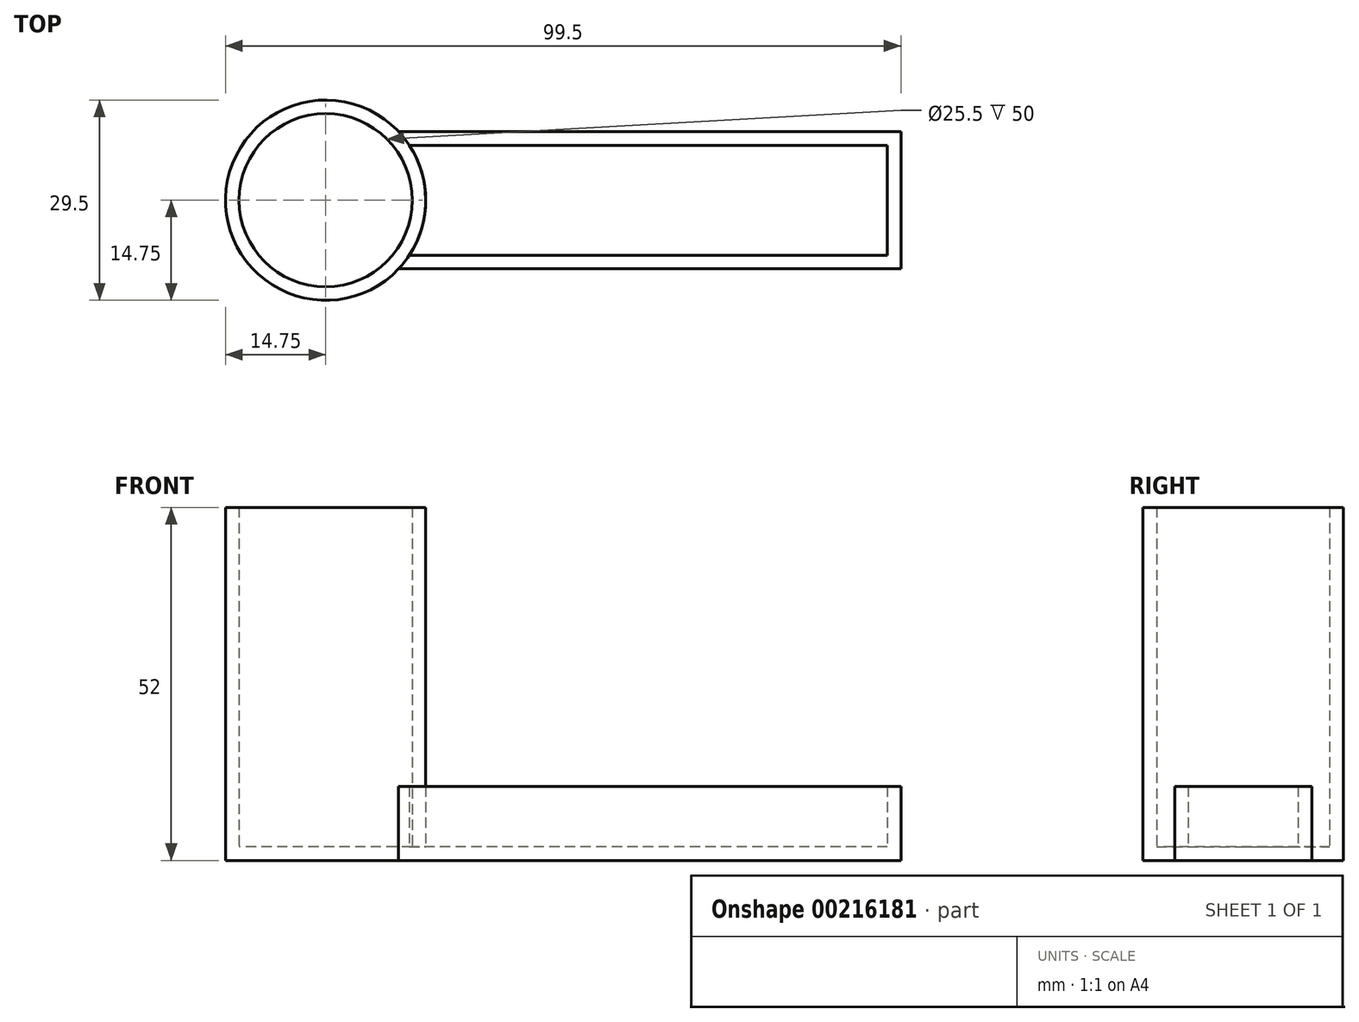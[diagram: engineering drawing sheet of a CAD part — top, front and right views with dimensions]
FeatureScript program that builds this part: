
annotation { "Feature Type Name" : "Feature", "Feature Type Description" : "" }
export const myFeature = defineFeature(function(context is Context, id is Id, definition is map)
    precondition{}
    {
        {
            var Q0;
            Q0=qCreatedBy(makeId("Top.planeOp"),FACE);
            var sketch = newSketch(context, id + "F0", { "sketchPlane" : qUnion([Q0])});
            skCircle(sketch, "E0", {"center": v(0, 0) * mm, "radius": 12.75 * mm});
            skCircle(sketch, "E1", {"center": v(0, 0) * mm, "radius": 14.75 * mm});
            skLineSegment(sketch, "E2", {"start": v(14.75, 0) * mm, "end": v(82.75, 0) * mm});
            skLineSegment(sketch, "E3", {"start": v(82.75, 0) * mm, "end": v(82.75, 8.1) * mm});
            skLineSegment(sketch, "E4", {"start": v(82.75, 0) * mm, "end": v(82.75, -8.1) * mm});
            skLineSegment(sketch, "E5", {"start": v(82.75, -8.1) * mm, "end": v(12.33, -8.1) * mm});
            skLineSegment(sketch, "E6", {"start": v(82.75, 8.1) * mm, "end": v(12.33, 8.1) * mm});
            skLineSegment(sketch, "E7", {"start": v(82.75, 8.1) * mm, "end": v(82.75, 10.1) * mm});
            skLineSegment(sketch, "E8", {"start": v(82.75, 10.1) * mm, "end": v(84.75, 10.1) * mm});
            skLineSegment(sketch, "E9", {"start": v(82.75, 10.1) * mm, "end": v(10.75, 10.1) * mm});
            skLineSegment(sketch, "E10", {"start": v(82.75, -8.1) * mm, "end": v(82.75, -10.1) * mm});
            skLineSegment(sketch, "E11", {"start": v(82.75, -10.1) * mm, "end": v(84.75, -10.1) * mm});
            skLineSegment(sketch, "E12", {"start": v(82.75, -10.1) * mm, "end": v(10.75, -10.1) * mm});
            skLineSegment(sketch, "E13", {"start": v(84.75, -10.1) * mm, "end": v(84.75, 10.1) * mm});
            skSolve(sketch);
        }
        {
            var Q0;
            {var subQ0=sQuery(id+"F0.wireOp",EDGE,"E6");Q0=makeQuery(id+"F0.imprint","IMPRINT",FACE,{"disambiguationData":[TD([[makeQuery(id+"F0.imprint","IMPRINT",EDGE,{"derivedFrom":subQ0}),-1.0]])]});}
            var Q1;
            Q1=makeQuery(id+"F0.imprint","IMPRINT",FACE,{"disambiguationData":[TD([[makeQuery(id+"F0.imprint","IMPRINT",EDGE,{"derivedFrom":sQuery(id+"F0.wireOp",EDGE,"E3")}),-1.0]])]});
            var Q2;
            {var subQ0=sQuery(id+"F0.wireOp",EDGE,"E5");Q2=makeQuery(id+"F0.imprint","IMPRINT",FACE,{"disambiguationData":[TD([[makeQuery(id+"F0.imprint","IMPRINT",EDGE,{"derivedFrom":subQ0}),1.0]])]});}
            extrude(context, id + "F1", {"entities" : qUnion([Q0, Q1, Q2]), "depth" : 10.9 * mm});
        }
        {
            var Q0;
            Q0=makeQuery(id+"F0.imprint","IMPRINT",FACE,{"disambiguationData":[TD([[makeQuery(id+"F0.imprint","IMPRINT",EDGE,{"derivedFrom":sQuery(id+"F0.wireOp",EDGE,"E0")}),-1.0]])]});
            extrude(context, id + "F2", {"entities" : qUnion([Q0]), "operationType" : NewBodyOperationType.ADD, "depth" : 52 * mm});
        }
        {
            var Q0;
            {var subQ0=sQuery(id+"F0.wireOp",EDGE,"E2");Q0=makeQuery(id+"F0.imprint","IMPRINT",FACE,{"disambiguationData":[TD([[makeQuery(id+"F0.imprint","IMPRINT",EDGE,{"derivedFrom":subQ0}),1.0]])]});}
            var Q1;
            {var subQ0=sQuery(id+"F0.wireOp",EDGE,"E2");Q1=makeQuery(id+"F0.imprint","IMPRINT",FACE,{"disambiguationData":[TD([[makeQuery(id+"F0.imprint","IMPRINT",EDGE,{"derivedFrom":subQ0}),-1.0]])]});}
            extrude(context, id + "F3", {"entities" : qUnion([Q0, Q1]), "operationType" : NewBodyOperationType.ADD, "depth" : 2 * mm});
        }
        {
            var Q0;
            Q0=makeQuery(id+"F0.imprint","IMPRINT",FACE,{"disambiguationData":[TD([[makeQuery(id+"F0.imprint","IMPRINT",EDGE,{"derivedFrom":sQuery(id+"F0.wireOp",EDGE,"E0")}),1.0]])]});
            extrude(context, id + "F4", {"entities" : qUnion([Q0]), "operationType" : NewBodyOperationType.ADD, "depth" : 2 * mm});
        }
    });
